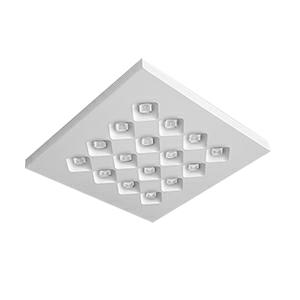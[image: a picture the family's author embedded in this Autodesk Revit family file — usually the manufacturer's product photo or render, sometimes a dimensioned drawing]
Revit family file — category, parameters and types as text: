
# Revit family: 3f_filippi_-_3f_diagon_3f_filippi_-_23024_a0686_-_3f_diagon_19w-840_596x596___corn_plaf__3b59
name_source: partatom
category: Lighting Fixtures
units: mm (PartAtom-declared; Revit-internal decimal feet)

## family parameters
Cut with Voids When Loaded = No
Host = Face
Light Source = No
Part Type = Normal
Room Calculation Point = No
Round Connector Dimension = Use Diameter
Shared = No

## types (1)
- 3F Filippi - 3F Dìagon (1 x LED, 3354 lm, 21 W, 4000 K)
    Apparent Load = 21 VA
    Approval mark = CE
    CIE Flux Codes = 67 96 100 100 100
    Color Rendering = 80
    Color Temperature = 4000 K
    Control Gear = Electronic ballast
    Default Elevation = 1800 mm
    Description = ILLUMINOTECHNICAL
Luminous efficiency 100% (DLOR 100%, ULOR 0%).
Initial luminous flux of the luminaire 3354 lm.
Direct symmetric distribution.
Installation Interdistance Transv.D = 1.39 x hu - Long.D = 1.39 x hu.
Average luminance <1500 cd/m² for radial angles >65°.
Tabular UGR (CIE 117 - 4H-8H; S=0.25H; 70/50/20): RUG 16.5 - 16.5.
Beam angle: 93° - 92°.
Luminous efficacy 160 lm/W.
Lifetime (L95/B10): 30000 h. (tq+25°C)
Lifetime (L90/B10): 50000 h. (tq+25°C)
Lifetime (L80/B10): 80000 h. (tq+25°C)
Lifetime (L75/B10): 100000 h. (tq+25°C)
Sudden decreased luminous flux after 50000 hours: 0% (C0).
Photobiological safety in compliance with IEC/TR 62778: RG0 risk exempt, (IEC 62471).
In compliance with IEC/EN 62722-2-1 - IEC/EN 62717 standards.

SOURCE
Squared LED module 19W/840.
Energy efficiency class (UE 2019/2020 - UE 2019/2015): C.
CIE 13.3 Colour rendering index: CRI >80 (R9 <50%).
IES TM-30 Fidelity Index: Rf = 84 Rg = 95.
CCT nominal colour temperature 4000 K.
Colour initial tolerance (MacAdam): SDCM 3.

MECHANICAL
Housing in hot-galvanised steel, painted in white polyester.
Honeycombed diagonal screen in white anti-glare polycarbonate.
Rhomboidal lenses with differentiated surfaces, etched and prismatic to optimise the orientation of the luminous flux, in transparent methacrylate (PMMA).
Luminaire with limited surface temperature. - D - (EN 60598-2-24)
Dimensions: 600x600 mm, height 40 mm. Weight 6.2 kg.
IP43 protection degree for exposed part, IP20 for recessed part.
Mechanical strength to impacts IK06 (1 joule).
Glow-wire test resistance 650°C.

ELECTRICAL
Halogen Free electronic wiring 230V-50/60Hz, power factor 0.90, THD <25%, constant output current, class I, 1 driver.
Power of the luminaire 21 W.
ENEC - CE.
SAFE FLICKER: PstLM=<1 and SVM=<0.4 (IEC TR 61547-1 and IEC TR 63158), to ensure a more comfortable and safe light.
Luminaire compliant with EN 60598-2-22 for power supply from a centralised emergency system CPSS (Central Power Supply System), not incorporated in the luminaire - high risk areas excluded. The default power and flux are 100% in AC and 100% in DC.
Ambient temperature from 0°C to +25°C.
Temperature class T6 max 85°C.
Quick connection.
Relative humidity UR: <85%.

INSTALLATION
Ceiling.
Height only 40 mm.
All accessories dedicated to this product are available on the Catalog and on our website www.3F-Filippi.com.

ACCESSORIES
A0686 - 596x596 Diagon frame for Ceiling installation.

APPLICATIONS
Environments: staterooms, with VDTs, offices.
Environments with exacting visual tasks, where diffused soft light for optimum visual comfort is required.

WARNING
Luminaire designed for disposal/recycling at end-of-life.
Replaceable (LED only) light source by a professional. Replaceable control gear by a professional.
    Height = 0 mm  [stored 0 ft]
    Lamp = 1 x LED
    Lamp Light Flux = 3354 lm
    Lamp Power = 21 W
    Lamp count = 1
    Length = 600 mm
    Lifetime = 50000 h
    Luminous efficacy = 160 lm/W
    Manufacturer = 3F Filippi
    ModVariant = No
    Model = 3F Filippi - 23024+A0686 - 3F Diagon 19W-840 596x596 + Corn.plaf.
    Mounting Place = Ceiling
    Mounting Type = Recessed
    Number of Poles = 1
    OnlyDefault = Yes
    Power Factor = 1
    Product Name = 3F Filippi - 3F Dìagon
    Product group = recessed luminaire
    ProductGroupID = 4
    Protection Class = Protection class I
    Protection Degree = IP 20
    RLX_Detail_Level = 1
    RLX_Emergency_Light_Flux = 0 lm
    RLX_Emergency_Type = 0
    RLX_Emergency_Type_DB = No
    RlxData = <blob elided: 96149 chars, md5=047b958d>
    Socket = socket
    Standby Power = 0 W
    System Light Flux = 3354 lm
    System Power = 21 W
    Type Comments = Product without accessories
    Type Image = 3ffilippi_3f_diagon__a0686.jpg
    URL = http://relux.com
    VarID = ---
    Voltage = 0 V
    Weight = 0.00 kg
    Width = 600 mm

note: [stored X ft] marks values corroborated as IEEE doubles in the binary element streams (Revit-internal decimal feet)

## geometry (parser evidence)
native form markers: Blend x4, Sweep x11
no freeform markers — native parametric forms only
